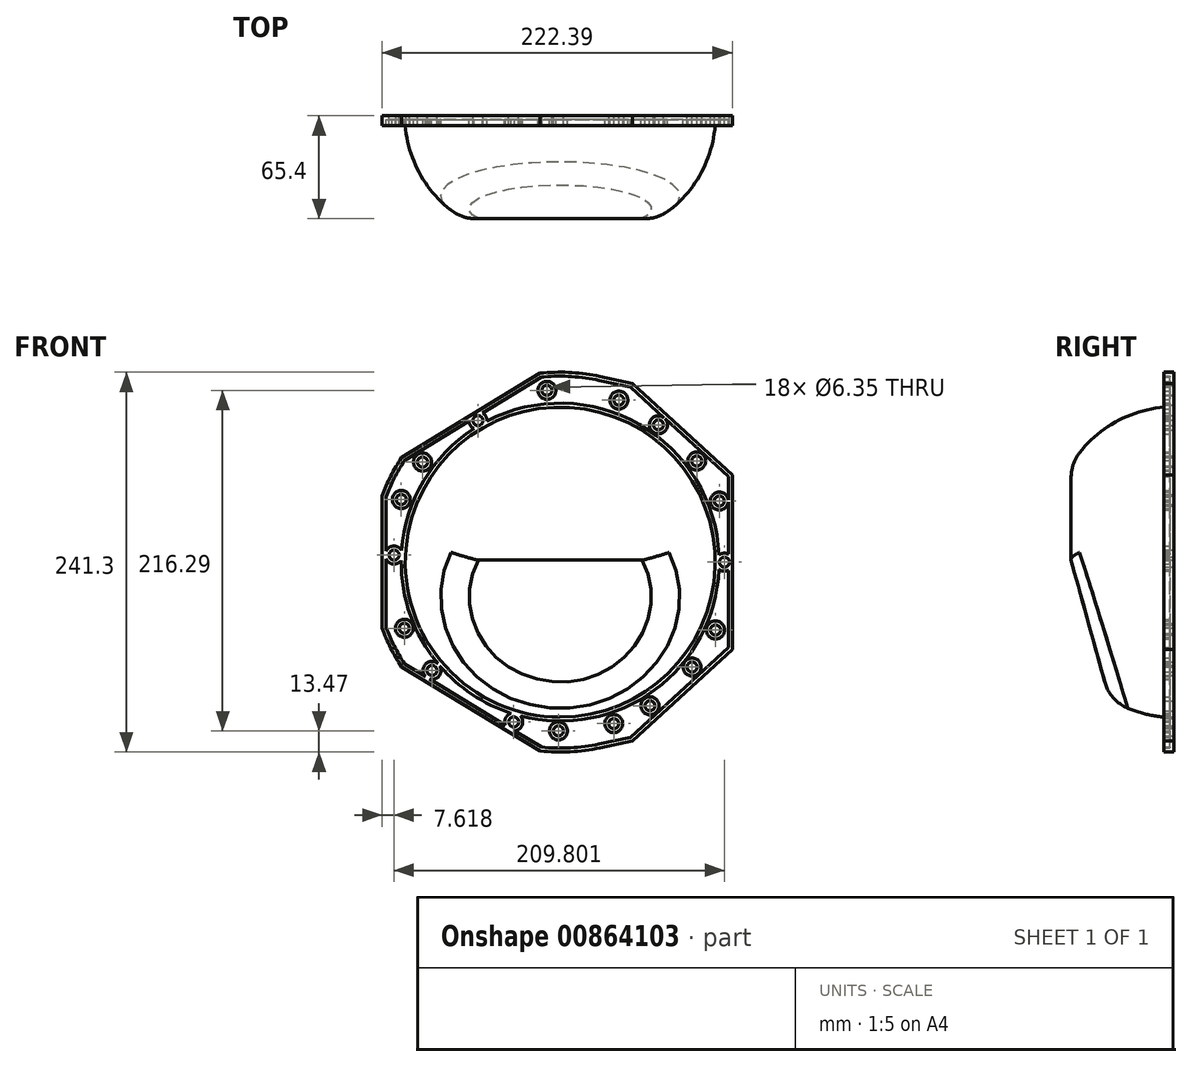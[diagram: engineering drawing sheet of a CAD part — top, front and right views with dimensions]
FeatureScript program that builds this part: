
annotation { "Feature Type Name" : "Feature", "Feature Type Description" : "" }
export const myFeature = defineFeature(function(context is Context, id is Id, definition is map)
    precondition{}
    {
        {
            var Q0;
            Q0=qCreatedBy(makeId("Front.planeOp"),FACE);
            var sketch = newSketch(context, id + "F0", { "sketchPlane" : qUnion([Q0])});
            skArc(sketch, "E0.0", {"start": v(-132.47, 119.29) * mm, "mid": v(-139.37, 107.4) * mm, "end": v(-144.88, 94.79) * mm});
            skLineSegment(sketch, "E0.1", {"start": v(-144.88, 94.79) * mm, "end": v(-144.88, 52.85) * mm});
            skLineSegment(sketch, "E0.2", {"start": v(-144.88, 52.85) * mm, "end": v(-144.88, 10.92) * mm});
            skArc(sketch, "E0.3", {"start": v(-144.88, 10.92) * mm, "mid": v(-139.37, -1.7) * mm, "end": v(-132.47, -13.59) * mm});
            skLineSegment(sketch, "E0.4", {"start": v(-132.47, -13.59) * mm, "end": v(-44.56, -67.12) * mm});
            skLineSegment(sketch, "E0.5", {"start": v(-6.48, 170.82) * mm, "end": v(14.11, 166.41) * mm});
            skArc(sketch, "E0.6", {"start": v(-6.48, 170.82) * mm, "mid": v(-16.21, 172.5) * mm, "end": v(-26.05, 173.37) * mm});
            skArc(sketch, "E0.7", {"start": v(-26.05, 173.37) * mm, "mid": v(-34.17, 173.48) * mm, "end": v(-42.27, 173.04) * mm});
            skLineSegment(sketch, "E0.9", {"start": v(14.11, 166.41) * mm, "end": v(77.5, 108.24) * mm});
            skLineSegment(sketch, "E0.10", {"start": v(77.5, 52.85) * mm, "end": v(77.5, 108.24) * mm});
            skLineSegment(sketch, "E0.11", {"start": v(77.5, -2.54) * mm, "end": v(77.5, 52.85) * mm});
            skLineSegment(sketch, "E0.12", {"start": v(14.11, -60.7) * mm, "end": v(77.5, -2.54) * mm});
            skLineSegment(sketch, "E0.13", {"start": v(-6.48, -65.12) * mm, "end": v(14.11, -60.7) * mm});
            skLineSegment(sketch, "E0.14", {"start": v(-132.47, 119.29) * mm, "end": v(-44.56, 172.82) * mm});
            skArc(sketch, "E0.15", {"start": v(-44.56, -67.12) * mm, "mid": v(-25.44, -67.63) * mm, "end": v(-6.48, -65.12) * mm});
            skCircle(sketch, "E1", {"center": v(-40.2, 161.96) * mm, "radius": 3.18 * mm});
            skCircle(sketch, "E2", {"center": v(5.49, 155.74) * mm, "radius": 3.18 * mm});
            skCircle(sketch, "E3", {"center": v(30.63, 140.06) * mm, "radius": 3.18 * mm});
            skCircle(sketch, "E4", {"center": v(54.97, 117.08) * mm, "radius": 3.18 * mm});
            skCircle(sketch, "E5", {"center": v(69.3, 91.67) * mm, "radius": 3.18 * mm});
            skCircle(sketch, "E6", {"center": v(72.54, 52.85) * mm, "radius": 3.18 * mm});
            skCircle(sketch, "E7", {"center": v(66.86, 9.75) * mm, "radius": 3.18 * mm});
            skCircle(sketch, "E8", {"center": v(52, -13.78) * mm, "radius": 3.18 * mm});
            skCircle(sketch, "E9", {"center": v(25.23, -38.38) * mm, "radius": 3.18 * mm});
            skCircle(sketch, "E10", {"center": v(2.24, -49.73) * mm, "radius": 3.18 * mm});
            skCircle(sketch, "E11", {"center": v(-32.9, -54.33) * mm, "radius": 3.18 * mm});
            skCircle(sketch, "E12", {"center": v(-61.3, -48.65) * mm, "radius": 3.18 * mm});
            skCircle(sketch, "E13", {"center": v(-113.2, -15.94) * mm, "radius": 3.18 * mm});
            skCircle(sketch, "E14", {"center": v(-130.77, 10.83) * mm, "radius": 3.18 * mm});
            skCircle(sketch, "E15", {"center": v(-137.26, 57.33) * mm, "radius": 3.18 * mm});
            skCircle(sketch, "E16", {"center": v(-132.7, 92.64) * mm, "radius": 3.18 * mm});
            skCircle(sketch, "E17", {"center": v(-119.2, 116.44) * mm, "radius": 3.18 * mm});
            skCircle(sketch, "E18", {"center": v(-84, 142.76) * mm, "radius": 3.18 * mm});
            skCircle(sketch, "E19.0", {"center": v(-31.76, 52.85) * mm, "radius": 98.43 * mm});
            skLineSegment(sketch, "E20", {"start": v(-44.56, 172.82) * mm, "end": v(-42.27, 173.04) * mm});
            skSolve(sketch);
        }
        {
            var Q0;
            Q0=makeQuery(id+"F0.imprint","IMPRINT",FACE,{"disambiguationData":[TD([[makeQuery(id+"F0.imprint","IMPRINT",EDGE,{"derivedFrom":sQuery(id+"F0.wireOp",EDGE,"E0.0")}),1.0]])]});
            extrude(context, id + "F1", {"entities" : qUnion([Q0]), "depth" : 6.35 * mm, "offsetDistance" : 25.4 * mm});
        }
        {
            var Q0;
            Q0=makeQuery(id+"F1.opExtrude","CAP_FACE",FACE,{"disambiguationData":[OSD([sQuery(id+"F0.wireOp",EDGE,"E0.0"),sQuery(id+"F0.wireOp",EDGE,"E0.1"),sQuery(id+"F0.wireOp",EDGE,"E0.2"),sQuery(id+"F0.wireOp",EDGE,"E0.3"),sQuery(id+"F0.wireOp",EDGE,"E0.4"),sQuery(id+"F0.wireOp",EDGE,"E0.5"),sQuery(id+"F0.wireOp",EDGE,"E0.6"),sQuery(id+"F0.wireOp",EDGE,"E0.7"),sQuery(id+"F0.wireOp",EDGE,"E0.9"),sQuery(id+"F0.wireOp",EDGE,"E0.10"),sQuery(id+"F0.wireOp",EDGE,"E0.11"),sQuery(id+"F0.wireOp",EDGE,"E0.12"),sQuery(id+"F0.wireOp",EDGE,"E0.13"),sQuery(id+"F0.wireOp",EDGE,"E0.14"),sQuery(id+"F0.wireOp",EDGE,"E0.15"),sQuery(id+"F0.wireOp",EDGE,"E1"),sQuery(id+"F0.wireOp",EDGE,"E2"),sQuery(id+"F0.wireOp",EDGE,"E3"),sQuery(id+"F0.wireOp",EDGE,"E4"),sQuery(id+"F0.wireOp",EDGE,"E5"),sQuery(id+"F0.wireOp",EDGE,"E6"),sQuery(id+"F0.wireOp",EDGE,"E7"),sQuery(id+"F0.wireOp",EDGE,"E8"),sQuery(id+"F0.wireOp",EDGE,"E9"),sQuery(id+"F0.wireOp",EDGE,"E10"),sQuery(id+"F0.wireOp",EDGE,"E11"),sQuery(id+"F0.wireOp",EDGE,"E12"),sQuery(id+"F0.wireOp",EDGE,"E13"),sQuery(id+"F0.wireOp",EDGE,"E14"),sQuery(id+"F0.wireOp",EDGE,"E15"),sQuery(id+"F0.wireOp",EDGE,"E16"),sQuery(id+"F0.wireOp",EDGE,"E17"),sQuery(id+"F0.wireOp",EDGE,"E18"),sQuery(id+"F0.wireOp",EDGE,"E19.0"),sQuery(id+"F0.wireOp",EDGE,"E20")])],"isStart":false});
            shell(context, id + "F2", {"entities" : qUnion([Q0]), "thickness" : 2.54 * mm});
        }
        {
            var Q0;
            Q0=makeQuery(id+"F0.imprint","IMPRINT",FACE,{"disambiguationData":[TD([[makeQuery(id+"F0.imprint","IMPRINT",EDGE,{"derivedFrom":sQuery(id+"F0.wireOp",EDGE,"E19.0")}),1.0]])]});
            extrude(context, id + "F3", {"entities" : qUnion([Q0]), "operationType" : NewBodyOperationType.ADD, "depth" : 76.2 * mm, "offsetDistance" : 25.4 * mm});
        }
        {
            var Q0;
            Q0=makeQuery(id+"F3.opExtrude","CAP_EDGE",EDGE,{"disambiguationData":[OSD([sQuery(id+"F0.wireOp",EDGE,"E19.0")])],"isStart":false});
            fillet(context, id + "F4", {"entities" : qUnion([Q0]), "radius" : 76.2 * mm, "tangentPropagation" : true, "allowEdgeOverflow" : false});
        }
        {
            var Q0;
            Q0=qCreatedBy(makeId("Right.planeOp"),FACE);
            var sketch = newSketch(context, id + "F5", { "sketchPlane" : qUnion([Q0])});
            skLineSegment(sketch, "E21.bottom", {"start": v(-65.4, 146.67) * mm, "end": v(-101.64, 146.67) * mm});
            skLineSegment(sketch, "E21.top", {"start": v(-65.4, -38.2) * mm, "end": v(-101.64, -38.2) * mm});
            skLineSegment(sketch, "E21.left", {"start": v(-65.4, 146.67) * mm, "end": v(-65.4, -38.2) * mm});
            skLineSegment(sketch, "E21.right", {"start": v(-101.64, 146.67) * mm, "end": v(-101.64, -38.2) * mm});
            skPoint(sketch, "E21.middle", {"position": v(-83.52, 54.24) * mm});
            skLineSegment(sketch, "E22", {"start": v(-65.4, 54.24) * mm, "end": v(-35.5, -54.2) * mm});
            skLineSegment(sketch, "E23", {"start": v(-35.5, -54.2) * mm, "end": v(-65.4, -38.2) * mm});
            skSolve(sketch);
        }
        {
            var Q0;
            {var subQ2=sQuery(id+"F5.wireOp",EDGE,"E22");Q0=makeQuery(id+"F5.imprint","IMPRINT",FACE,{"disambiguationData":[TD([[makeQuery(id+"F5.imprint","IMPRINT",EDGE,{"derivedFrom":subQ2}),-1.0]])]});}
            var Q1;
            {var subQ3=sQuery(id+"F5.wireOp",EDGE,"E21.bottom");Q1=makeQuery(id+"F5.imprint","IMPRINT",FACE,{"disambiguationData":[TD([[makeQuery(id+"F5.imprint","IMPRINT",EDGE,{"derivedFrom":subQ3}),1.0]])]});}
            extrude(context, id + "F6", {"entities" : qUnion([Q0, Q1]), "operationType" : NewBodyOperationType.REMOVE, "oppositeDirection" : true, "depth" : 381 * mm, "offsetDistance" : 25.4 * mm, "symmetric" : true});
        }
        {
            var Q0;
            Q0=makeQuery(id+"F6.boolean.opBoolean","INTERSECT",EDGE,{"derivedFrom":[makeQuery(id+"F4.opFillet","BLEND_FACE",FACE,{"disambiguationData":[OSD([sQuery(id+"F0.wireOp",EDGE,"E19.0")])]}),makeQuery(id+"F6.opExtrude","SWEPT_FACE",FACE,{"disambiguationData":[OSD([sQuery(id+"F5.wireOp",EDGE,"E21.left")])]})]});
            var Q1;
            Q1=makeQuery(id+"F6.boolean.opBoolean","INTERSECT",EDGE,{"derivedFrom":[makeQuery(id+"F4.opFillet","BLEND_FACE",FACE,{"disambiguationData":[OSD([sQuery(id+"F0.wireOp",EDGE,"E19.0")])]}),makeQuery(id+"F6.opExtrude","SWEPT_FACE",FACE,{"disambiguationData":[OSD([sQuery(id+"F5.wireOp",EDGE,"E22")])]})]});
            fillet(context, id + "F7", {"entities" : qUnion([Q0, Q1]), "radius" : 25.4 * mm, "tangentPropagation" : true, "allowEdgeOverflow" : false});
        }
    });
